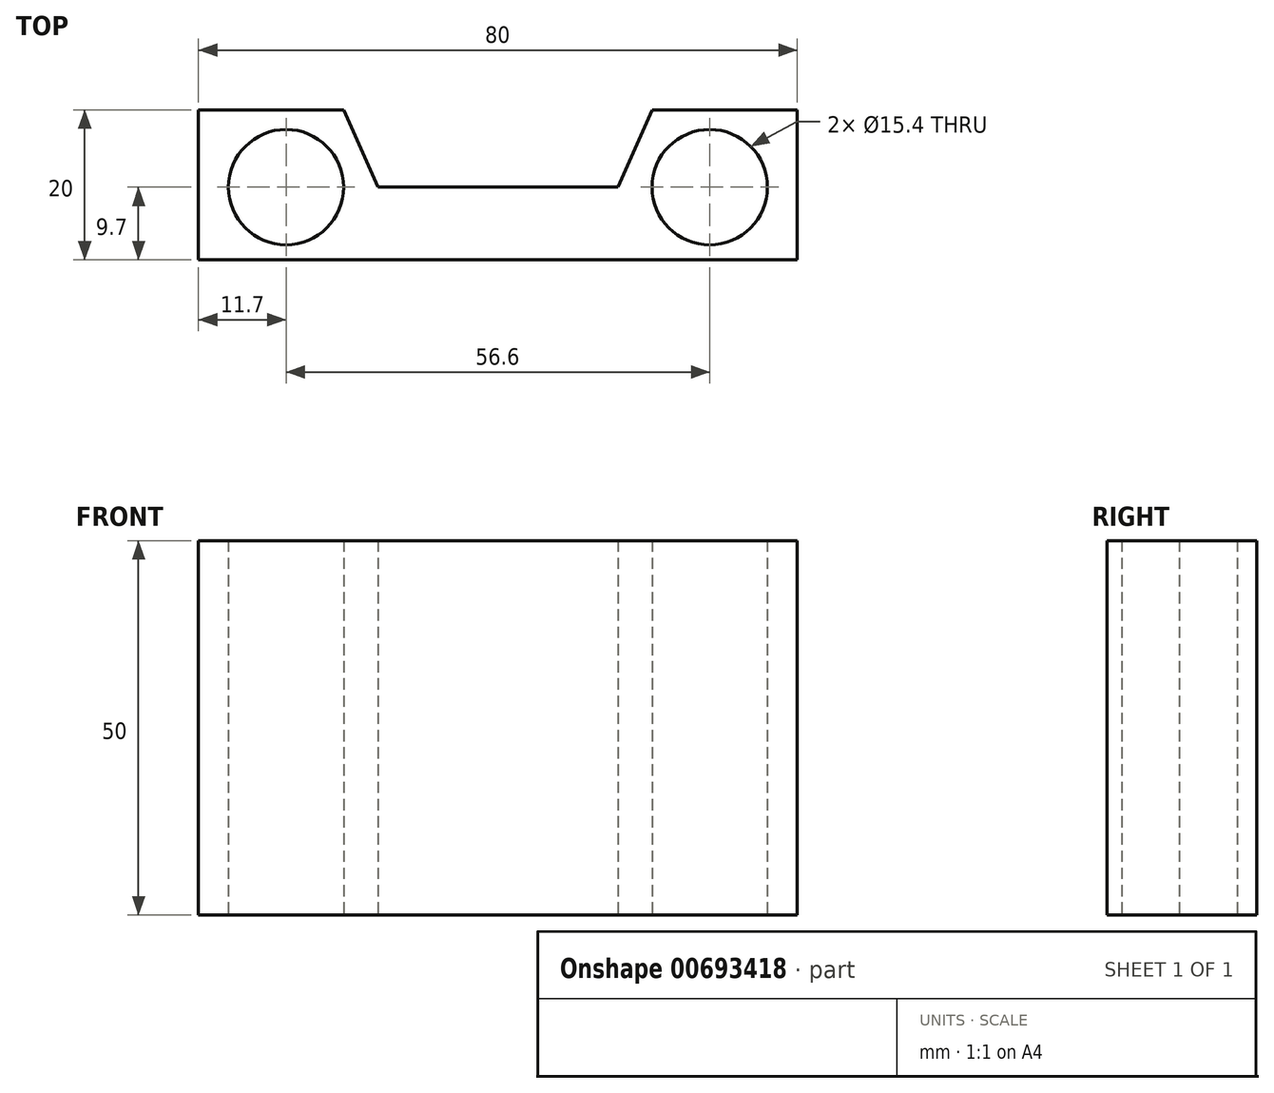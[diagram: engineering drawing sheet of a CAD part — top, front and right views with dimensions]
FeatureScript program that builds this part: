
annotation { "Feature Type Name" : "Feature", "Feature Type Description" : "" }
export const myFeature = defineFeature(function(context is Context, id is Id, definition is map)
    precondition{}
    {
        {
            var Q0;
            Q0=qCreatedBy(makeId("Top.planeOp"),FACE);
            var sketch = newSketch(context, id + "F0", { "sketchPlane" : qUnion([Q0])});
            skLineSegment(sketch, "E0.bottom", {"start": v(-40, 0) * mm, "end": v(40, 0) * mm});
            skLineSegment(sketch, "E0.top", {"start": v(-40, 20) * mm, "end": v(40, 20) * mm});
            skLineSegment(sketch, "E0.left", {"start": v(-40, 0) * mm, "end": v(-40, 20) * mm});
            skLineSegment(sketch, "E0.right", {"start": v(40, 0) * mm, "end": v(40, 20) * mm});
            skCircle(sketch, "E1", {"center": v(-28.3, 9.7) * mm, "radius": 7.7 * mm});
            skLineSegment(sketch, "E2", {"start": v(0, 20) * mm, "end": v(0, 0) * mm, "construction": true});
            skCircle(sketch, "E3.MirrorC", {"center": v(28.3, 9.7) * mm, "radius": 7.7 * mm});
            skLineSegment(sketch, "E4", {"start": v(-20.6, 9.7) * mm, "end": v(20.6, 9.7) * mm});
            skLineSegment(sketch, "E5", {"start": v(16.01, 9.7) * mm, "end": v(20.6, 20) * mm});
            skLineSegment(sketch, "E6.MirrorCS", {"start": v(-16.01, 9.7) * mm, "end": v(-20.6, 20) * mm});
            skSolve(sketch);
        }
        {
            var Q0;
            Q0=makeQuery(id+"F0.imprint","IMPRINT",FACE,{"disambiguationData":[TD([[makeQuery(id+"F0.imprint","IMPRINT",EDGE,{"derivedFrom":sQuery(id+"F0.wireOp",EDGE,"E0.bottom")}),1.0]])]});
            extrude(context, id + "F1", {"entities" : qUnion([Q0]), "depth" : 50 * mm, "offsetDistance" : 25 * mm});
        }
    });
